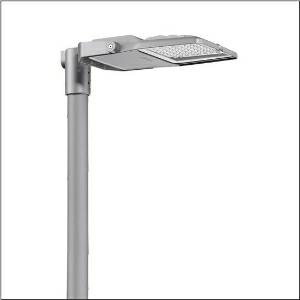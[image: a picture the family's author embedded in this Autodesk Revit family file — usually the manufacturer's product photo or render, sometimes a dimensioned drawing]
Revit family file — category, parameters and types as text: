
# Revit family: floodlight_fl_21_iq_mini___pl43_5xa7771b2a3a_6d21
name_source: partatom
category: Lighting Fixtures
units: mm (PartAtom-declared; Revit-internal decimal feet)

## family parameters
Cut with Voids When Loaded = No
Host = Face
Light Source = No
Part Type = Normal
Room Calculation Point = No
Round Connector Dimension = Use Diameter
Shared = No

## types (1)
- --- (1 x LED, 6400 lm, 45.5 W, 3000K)
    Apparent Load = 46 VA
    CIE Flux Codes = 27 78 99 100 100
    Color Rendering = 70
    Color Temperature = 3000K
    Default Elevation = 1800 mm
    Description = Floodlight FL 21 iQ mini, floodlight, primary light control with lens, of PMMA, primary optical cover: protective disc, of toughened safety glass, transparent, light distribution: PL43, light emission: direct distribution, installation type: surface-mounted, lamps: LED, High Power LED, rated values: 6.400lm | 45,5W | 140,7lm/W (begin service life); end service life: 6.400lm | 48W; at 50% lumin. flux: 3.200lm | 21,5W | 148,8lm/W, colour temperature: 3000K, colour rendering: CRI > 70, light colour: 730, light setting 1 begin service life: 100% | 6.400lm | 45,5W | 140,7lm/W | 3.000K, light setting 1 end service life: 48W, further light settings possible, control: Auto-Match, Temp-Guard, Lumen-Switch, Night-Set, Smart-Wire, Light-Fading, Desk-Remote (wireless, voltage-free reading and setting of iQ features in the workshop via application-optimized NFC function/RFID function), optimised constant luminous flux control (CLO 2.0), pre-setting: linear dimming characteristic, with terminal, 6-pole, mains connection: 220..240V, AC, 50/60Hz, luminaire housing, of diecast aluminium, powder-coated, SITECO metallic grey (DB 702S), corrosivity category C5 mid according to DIN EN ISO 12944suitable for swimming poolschlorine-resistant, sealing non-destructively replaceable, please order mast flange separately, mast bracket, of steel, galvanised, powder-coated, SITECO metallic grey (DB 702S), protection rating (complete): IP66, insulation class (complete): insulation class II (safety insulation), certification: CE, ENEC, VDE, protection symbol: D, impact resistance: IK08, permissible operating ambient temperature: -40..+40°C, permissible operating ambient temperature for outdoor applications: -40..+50°C, standard: DIN EN 12944, LABS conformity tested according to VDMA 24364:2018-05, packaging unit: 1 piece

Light Distribution: PL43
    Height = 70 mm
    Lamp = 1 x LED
    Lamp Light Flux = 6400 lm
    Lamp Power = 45.5 W
    Lamp count = 1
    Length = 485 mm
    Luminous efficacy = 141 lm/W
    Manufacturer = Siteco
    ModVariant = No
    Model = 5XA7771B2A3A
    Number of Poles = 1
    OnlyDefault = Yes
    Power Factor = 1
    Product Name = Floodlight FL 21 iQ mini | PL43
    Product group = floodlight | pylon annexe
    ProductGroupID = 6201
    Protection Class = Protection class II
    Protection Degree = IP 66
    RLX_Detail_Level = 1
    RLX_Emergency_Light_Flux = 0 lm
    RLX_Emergency_Type = 0
    RLX_Emergency_Type_DB = No
    RlxData = <blob elided: 101401 chars, md5=9e22a71a>
    Socket = socket
    Standby Power = 0 W
    System Light Flux = 6400 lm
    System Power = 46 W
    Type Comments = factory setting: luminous flux: 100 % | dim-lin: 254 | 463 mA
    Type Image = l_1007125.jpg
    URL = http://relux.com
    VarID = @adj_162467
    Voltage = 0 V
    Weight = 0.00 kg
    Width = 337 mm

## geometry (parser evidence)
native form markers: Blend x4, Sweep x11
no freeform markers — native parametric forms only
